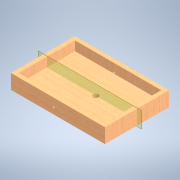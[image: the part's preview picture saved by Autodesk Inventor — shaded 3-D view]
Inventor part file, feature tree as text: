
AUTODESK INVENTOR PART (.ipt)
format: ipt  version: 2020 (Build 240168000, 168)  size: 139,776 bytes
history: native  units: in
note: dims shown in document units (in); Inventor stores cm internally (conversion verified against a paired STEP export)
features: extrude x4, sketch x4, plane x1
ambient origin geometry x8: Origin, YZ Plane, XZ Plane, XY Plane, X Axis, Y Axis, Z Axis, Center Point
bodies: Solid1 (feature_tree)
feature tree (9):
  extrude  "Extrusion1"  Depth=13.9764in TaperAngle=0.0deg
  extrude  "Extrusion3"  TaperAngle=0.0deg  [1 undecoded]
  extrude  "Extrusion4"  Depth=1.378in TaperAngle=0.0deg
  extrude  "Extrusion5"  Depth=13.9764in
  plane  "Work Plane1"
  sketch  "Sketch1"  dims[d0=2.1654in d1=9.5276in d2=13.9764in d3=0.0in]
  sketch  "Sketch3"  dims[d8=0.7874in d9=0.0in d10=0.0in]
  sketch  "Sketch4"  dims[d11=0.5906in d12=0.5906in d13=1.378in d14=0.0in]
  sketch  "Sketch5"  dims[d15=0.2362in d16=0.0in d17=0.0in d18=6.3544in d19=13.9764in d20=0.9092in d21=-4.7638in]
note: 1 required parameter value undecoded (feature->parameter linkage not recoverable at this tier; creation-order binding heuristic only, values carry confidence <= 0.55)
